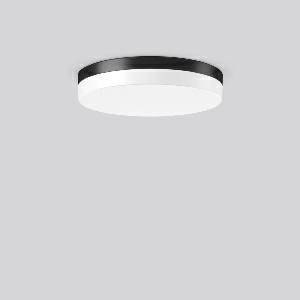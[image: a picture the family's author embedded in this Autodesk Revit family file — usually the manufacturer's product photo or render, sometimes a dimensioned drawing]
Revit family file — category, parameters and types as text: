
# Revit family: flat_slim_round_312632_0031_730_a5b0
name_source: partatom
category: Lighting Fixtures
units: mm (PartAtom-declared; Revit-internal decimal feet)

## family parameters
Cut with Voids When Loaded = No
Host = Face
Light Source = No
Part Type = Normal
Room Calculation Point = No
Round Connector Dimension = Use Diameter
Shared = No

## types (1)
- MultiLumen 1 830 (1 x LED Modul 830, 2400 lm, 3000)
    Apparent Load = 20 VA
    CIE Flux Codes = 39 70 90 83 100
    Color Rendering = 80
    Color Temperature = 3000
    Default Elevation = 1800 mm
    Height = 70 mm
    Lamp = 1 x LED Modul 830
    Lamp Light Flux = 2400 lm
    Lamp count = 1
    Length = 400 mm
    Lifetime = 50000 h
    Luminous efficacy = 120 lm/W
    Manufacturer = RZB
    ModVariant = No
    Model = 312632.0031.730
    Mounting Place = Ceiling
    Mounting Type = Surface mounted
    Number of Poles = 1
    OnlyDefault = Yes
    Power Factor = 1
    Product Name = FLAT SLIM round
    Product group = Surface mounted ceiling and wall luminaires
    ProductGroupID = 305
    Protection Class = Protection class I
    Protection Degree = Degree of protection
    RLX_Detail_Level = 1
    RLX_Emergency_Light_Flux = 0 lm
    RLX_Emergency_Type = 0
    RLX_Emergency_Type_DB = No
    RlxData = <blob elided: 21469 chars, md5=ab7b5234>
    Socket = socket
    Standby Power = 0 W
    System Light Flux = 2400 lm
    System Power = 20 W
    Type Comments = MultiLumen 1 830
    Type Image = 312631.0031.jpg
    URL = http://relux.com
    VarID = multilumen_1_830
    Voltage = 0 V
    Weight = 0.00 kg
    Width = 0 mm  [stored 0 ft]

note: [stored X ft] marks values corroborated as IEEE doubles in the binary element streams (Revit-internal decimal feet)

## geometry (parser evidence)
native form markers: Blend x4, Sweep x14
no freeform markers — native parametric forms only
